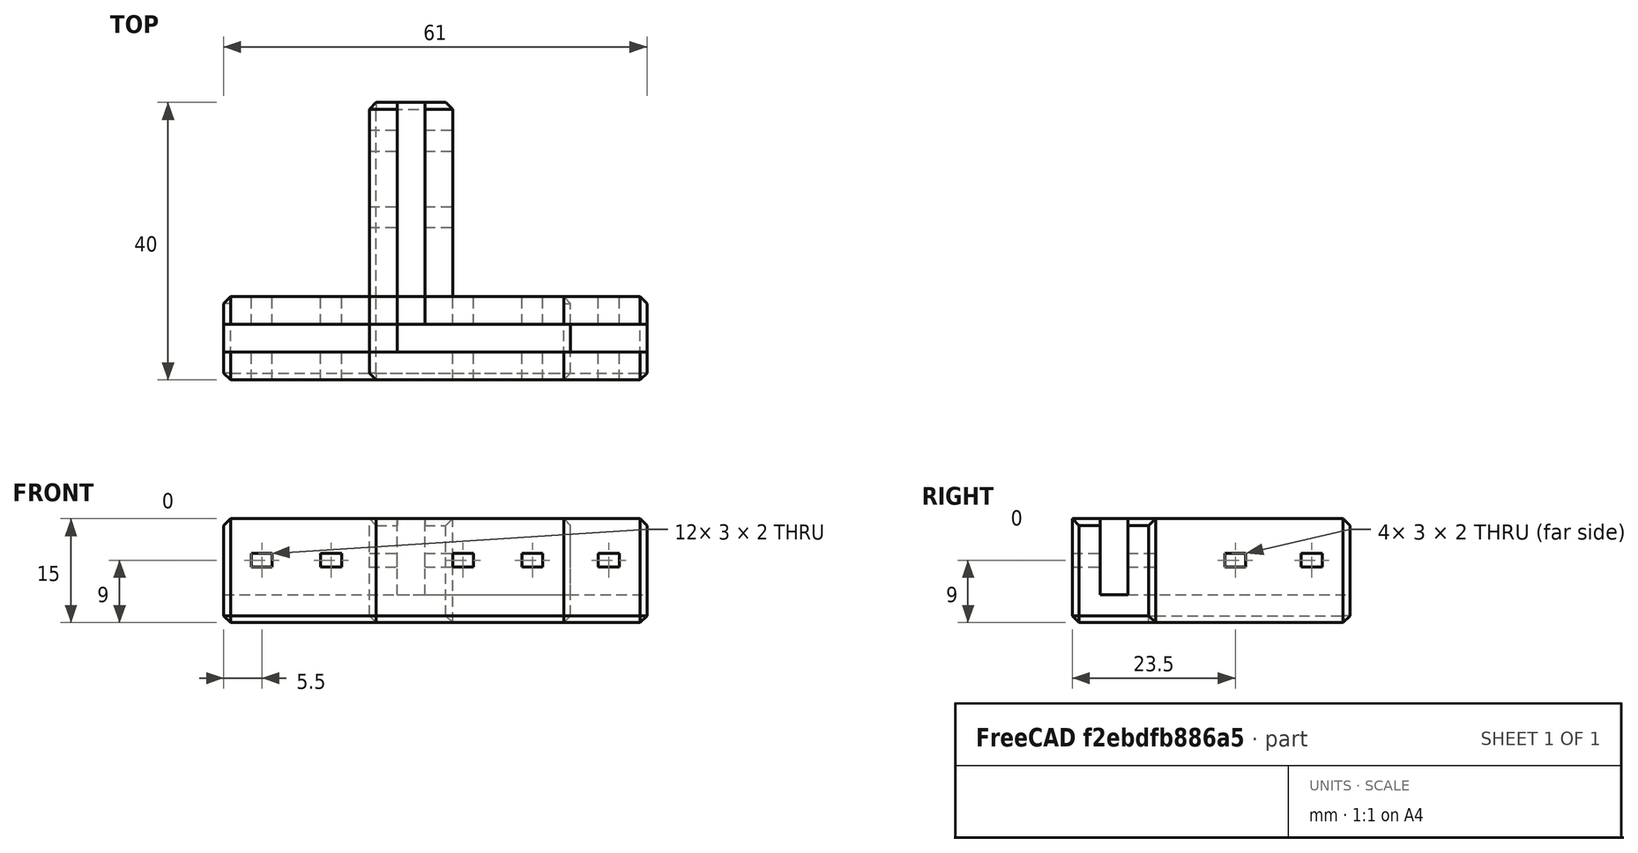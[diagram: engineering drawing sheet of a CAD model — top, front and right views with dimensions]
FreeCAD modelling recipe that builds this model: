
FCSTD DOCUMENT  (FreeCAD 0.18R16146 (Git))
Label: mesh-connector
License: All rights reserved
LicenseURL: http://en.wikipedia.org/wiki/All_rights_reserved
objects: Part::Box×14, Part::MultiFuse×4, Part::Cut×4, Part::Chamfer×2
note: 24 computed .brp shape members not serialized (recipe doc carries the construction recipe); baked Part::Feature solids carry a one-line shape summary decoded from their .brp

FEATURE [Part::Box] Box  label="Cube"
  AttacherType = Attacher::AttachEngine3D
  Height = 11
  Length = 36
  Placement = pos=(0,0,4) rot=(0,0,1;0rad)
  Width = 4
FEATURE [Part::Box] Box001  label="Cube001"
  AttacherType = Attacher::AttachEngine3D
  Height = 11
  Length = 4
  Placement = pos=(0,0,4) rot=(0,0,1;0rad)
  Width = 36
FEATURE [Part::Box] Box002  label="Cube002"
  AttacherType = Attacher::AttachEngine3D
  Height = 15
  Length = 12
  Placement = pos=(-4,-4,0) rot=(0,0,1;0rad)
  Width = 40
FEATURE [Part::Box] Box003  label="Cube003"
  AttacherType = Attacher::AttachEngine3D
  Height = 15
  Length = 40
  Placement = pos=(-4,-4,0) rot=(0,0,1;0rad)
  Width = 12
FEATURE [Part::Box] Box004  label="Cube004"
  AttacherType = Attacher::AttachEngine3D
  Height = 2
  Length = 15
  Placement = pos=(-5,18,8) rot=(0,0,1;0rad)
  Width = 3
FEATURE [Part::Box] Box005  label="Cube005"
  AttacherType = Attacher::AttachEngine3D
  Height = 2
  Length = 3
  Placement = pos=(18,-5,8) rot=(0,0,1;0rad)
  Width = 15
FEATURE [Part::Box] Box006  label="Cube006"
  AttacherType = Attacher::AttachEngine3D
  Height = 11
  Length = 50
  Placement = pos=(0,0,4) rot=(0,0,1;0rad)
  Width = 4
FEATURE [Part::Box] Box007  label="Cube007"
  AttacherType = Attacher::AttachEngine3D
  Height = 15
  Length = 50
  Placement = pos=(0,-4,0) rot=(0,0,1;0rad)
  Width = 12
FEATURE [Part::Box] Box008  label="Cube008"
  AttacherType = Attacher::AttachEngine3D
  Height = 2
  Length = 3
  Placement = pos=(18,-8,0) rot=(0,0,1;0rad)
  Width = 20
FEATURE [Part::Box] Box009  label="Cube009"
  AttacherType = Attacher::AttachEngine3D
  Height = 2
  Length = 3
  Placement = pos=(-21,-8,0) rot=(0,0,1;0rad)
  Width = 20
FEATURE [Part::Box] Box010  label="Cube010"
  AttacherType = Attacher::AttachEngine3D
  Height = 2
  Length = 3
  Placement = pos=(-11,-8,0) rot=(0,0,1;0rad)
  Width = 20
FEATURE [Part::Box] Box011  label="Cube011"
  AttacherType = Attacher::AttachEngine3D
  Height = 2
  Length = 3
  Placement = pos=(8,-8,0) rot=(0,0,1;0rad)
  Width = 20
FEATURE [Part::MultiFuse] Fusion003
  Placement = pos=(0,0,8) rot=(0,0,1;0rad)
  Shapes = -> [Box011,Box010,Box009,Box008]
FEATURE [Part::Chamfer] Chamfer001
  Base = -> Box007
  Edges = 10 edges r=1: [Edge1,Edge2,Edge3,Edge4,Edge5,Edge6,Edge7,Edge8,Edge9,Edge11]
FEATURE [Part::Cut] Cut002
  Base = -> Chamfer001
  Placement = pos=(-25,0,0) rot=(0,0,1;0rad)
  Tool = -> Box006
FEATURE [Part::Cut] Cut003  label="I"
  Base = -> Cut002
  Tool = -> Fusion003
FEATURE [Part::MultiFuse] Fusion
  Shapes = -> [Box001,Box]
FEATURE [Part::MultiFuse] Fusion004
  Shapes = -> [Box002,Box003]
FEATURE [Part::Chamfer] Chamfer
  Base = -> Fusion004
  Edges = 13 edges r=1: [Edge1,Edge4,Edge5,Edge11,Edge12,Edge15,Edge16,Edge18,Edge21,Edge22,Edge23,Edge26,Edge27]
FEATURE [Part::Cut] Cut
  Base = -> Chamfer
  Tool = -> Fusion
FEATURE [Part::Box] Box012  label="Cube012"
  AttacherType = Attacher::AttachEngine3D
  Height = 2
  Length = 15
  Placement = pos=(-5,29,8) rot=(0,0,1;0rad)
  Width = 3
FEATURE [Part::Box] Box013  label="Cube013"
  AttacherType = Attacher::AttachEngine3D
  Height = 2
  Length = 3
  Placement = pos=(29,-5,8) rot=(0,0,1;0rad)
  Width = 15
FEATURE [Part::MultiFuse] Fusion005
  Shapes = -> [Box013,Box012,Box004,Box005]
FEATURE [Part::Cut] Cut004
  Base = -> Cut
  Tool = -> Fusion005
